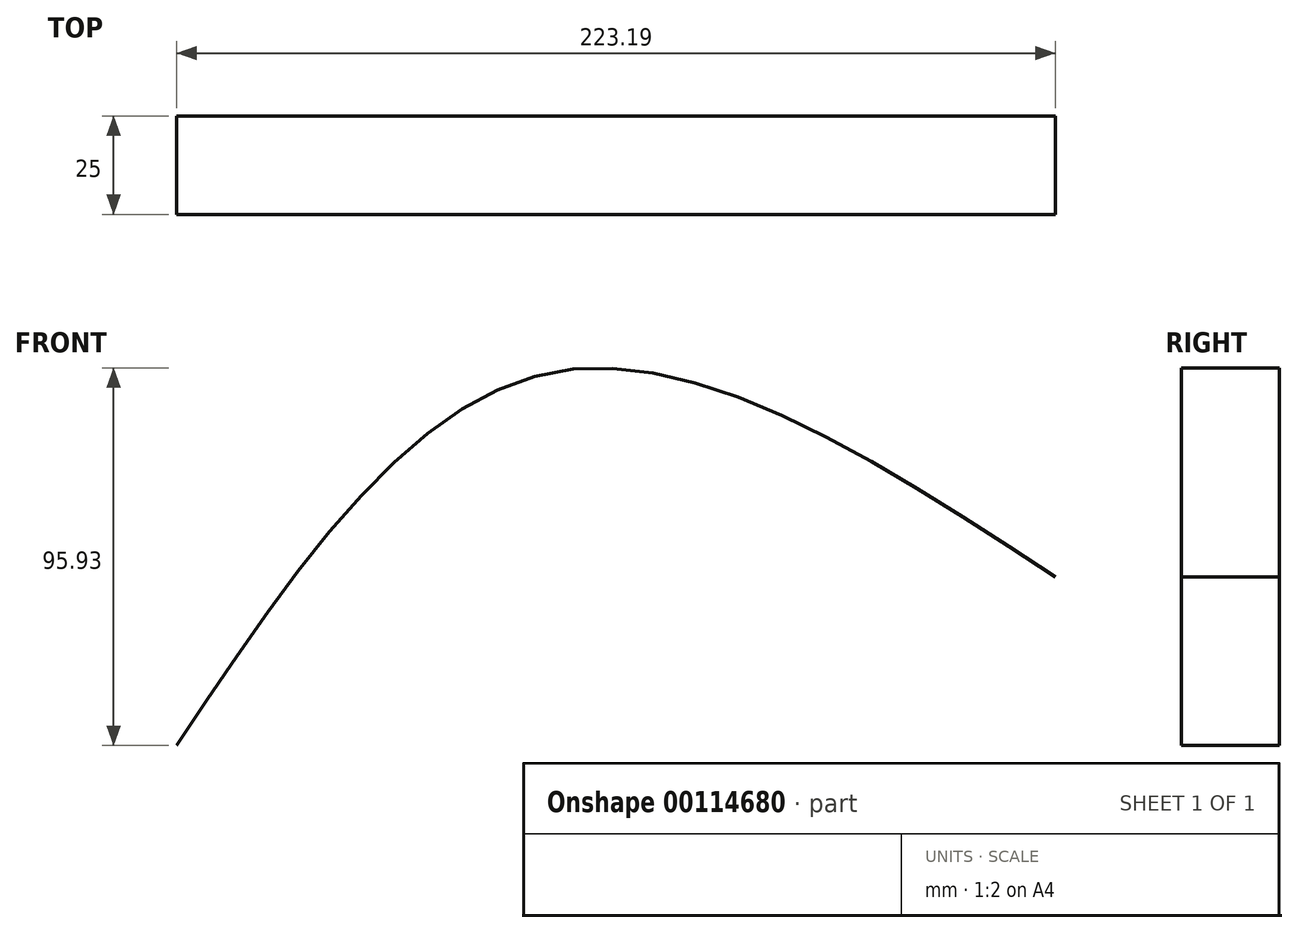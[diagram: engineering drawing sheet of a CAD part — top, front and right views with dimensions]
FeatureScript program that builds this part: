
annotation { "Feature Type Name" : "Feature", "Feature Type Description" : "" }
export const myFeature = defineFeature(function(context is Context, id is Id, definition is map)
    precondition{}
    {
        {
            var Q0;
            Q0=qCreatedBy(makeId("Front.planeOp"),FACE);
            var sketch = newSketch(context, id + "F0", { "sketchPlane" : qUnion([Q0])});
            skFitSpline(sketch, "E0", {"points": [v(-94.86, -94.73) * mm, v(0, 0) * mm, v(128.33, -51.85) * mm], "startDerivative": vector(175.52, 263.86) * mm, "endDerivative": vector(270.6, -176.94) * mm});
            skSolve(sketch);
        }
        {
            var Q0;
            Q0=sQuery(id+"F0.wireOp",EDGE,"E0");
            extrude(context, id + "F1", {"bodyType" : ToolBodyType.SURFACE, "surfaceEntities" : qUnion([Q0]), "depth" : 25 * mm});
        }
    });
